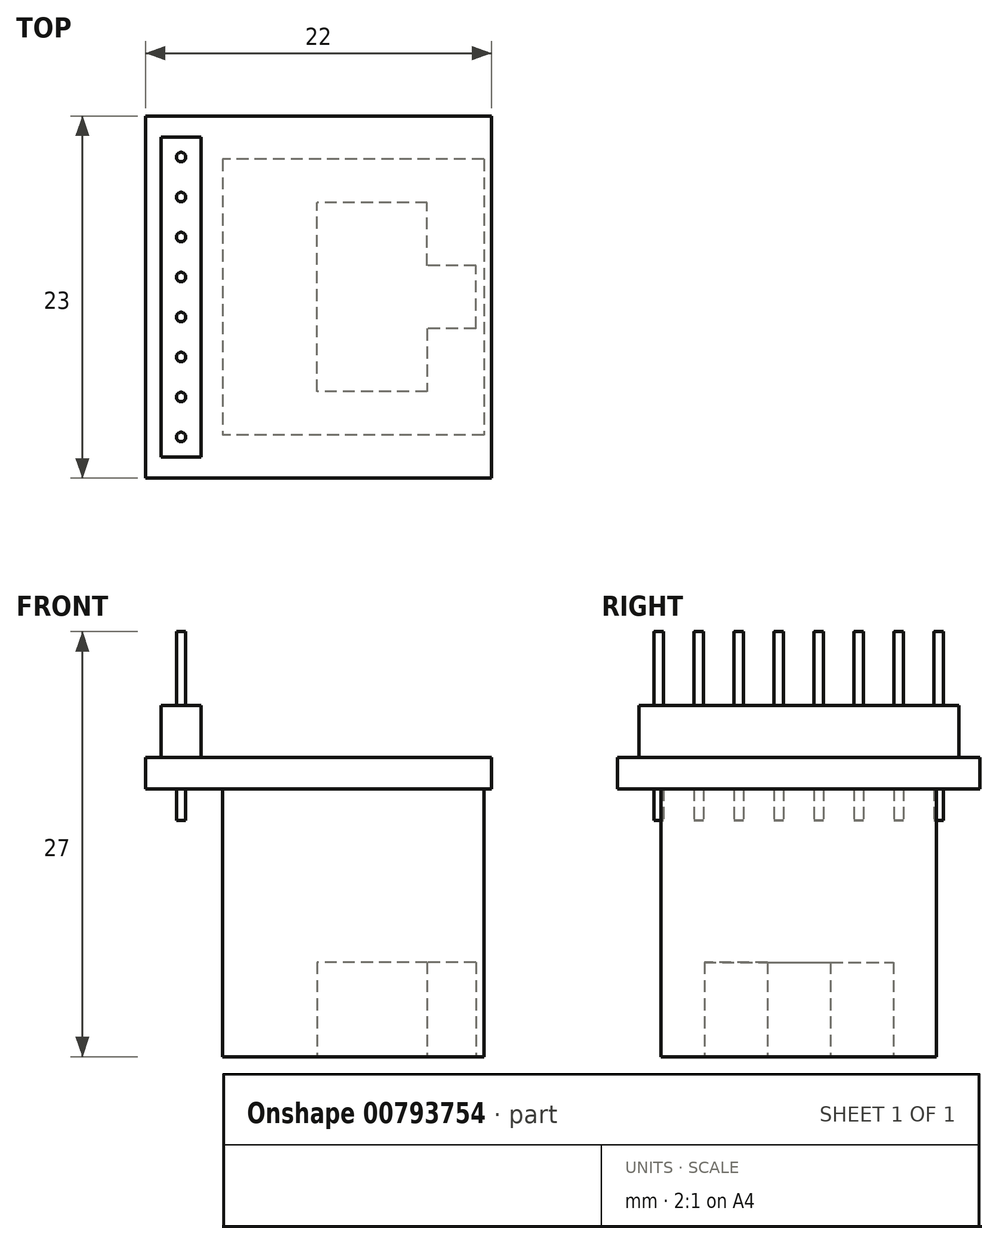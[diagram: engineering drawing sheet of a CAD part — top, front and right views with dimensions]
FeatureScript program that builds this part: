
annotation { "Feature Type Name" : "Feature", "Feature Type Description" : "" }
export const myFeature = defineFeature(function(context is Context, id is Id, definition is map)
    precondition{}
    {
        {
            var Q0;
            Q0=qCreatedBy(makeId("Top.planeOp"),FACE);
            var sketch = newSketch(context, id + "F0", { "sketchPlane" : qUnion([Q0])});
            skLineSegment(sketch, "E0.bottom", {"start": v(8.3, 8.75) * mm, "end": v(-8.3, 8.75) * mm});
            skLineSegment(sketch, "E0.top", {"start": v(8.3, -8.75) * mm, "end": v(-8.3, -8.75) * mm});
            skLineSegment(sketch, "E0.left", {"start": v(8.3, 8.75) * mm, "end": v(8.3, -8.75) * mm});
            skLineSegment(sketch, "E0.right", {"start": v(-8.3, 8.75) * mm, "end": v(-8.3, -8.75) * mm});
            skPoint(sketch, "E0.middle", {"position": v(0, 0) * mm});
            skSolve(sketch);
        }
        {
            var Q0;
            Q0=makeQuery(id+"F0.imprint","IMPRINT",FACE,{"disambiguationData":[TD([[makeQuery(id+"F0.imprint","IMPRINT",EDGE,{"derivedFrom":sQuery(id+"F0.wireOp",EDGE,"E0.bottom")}),1.0]])]});
            extrude(context, id + "F1", {"entities" : qUnion([Q0]), "depth" : 17 * mm, "offsetDistance" : 25 * mm});
        }
        {
            var Q0;
            Q0=makeQuery(id+"F1.opExtrude","CAP_FACE",FACE,{"disambiguationData":[OSD([sQuery(id+"F0.wireOp",EDGE,"E0.bottom"),sQuery(id+"F0.wireOp",EDGE,"E0.top"),sQuery(id+"F0.wireOp",EDGE,"E0.left"),sQuery(id+"F0.wireOp",EDGE,"E0.right")])],"isStart":true});
            var sketch = newSketch(context, id + "F2", { "sketchPlane" : qUnion([Q0])});
            skLineSegment(sketch, "E1", {"start": v(8.3, 0) * mm, "end": v(-8.3, 0) * mm, "construction": true});
            skLineSegment(sketch, "E2", {"start": v(7.8, 0) * mm, "end": v(7.8, -2) * mm});
            skLineSegment(sketch, "E3", {"start": v(7.8, -2) * mm, "end": v(4.7, -2) * mm});
            skLineSegment(sketch, "E4", {"start": v(4.7, -2) * mm, "end": v(4.7, -6) * mm});
            skLineSegment(sketch, "E5", {"start": v(4.7, -6) * mm, "end": v(-2.3, -6) * mm});
            skLineSegment(sketch, "E6", {"start": v(-2.3, -6) * mm, "end": v(-2.3, 0) * mm});
            skLineSegment(sketch, "E7.MirrorCS", {"start": v(7.8, 0) * mm, "end": v(7.8, 2) * mm});
            skLineSegment(sketch, "E8.MirrorCS", {"start": v(7.8, 2) * mm, "end": v(4.7, 2) * mm});
            skLineSegment(sketch, "E9.MirrorCS", {"start": v(4.7, 2) * mm, "end": v(4.7, 6) * mm});
            skLineSegment(sketch, "E10.MirrorCS", {"start": v(4.7, 6) * mm, "end": v(-2.3, 6) * mm});
            skLineSegment(sketch, "E11.MirrorCS", {"start": v(-2.3, 6) * mm, "end": v(-2.3, 0) * mm});
            skSolve(sketch);
        }
        {
            var Q0;
            Q0=makeQuery(id+"F2.imprint","IMPRINT",FACE,{"disambiguationData":[TD([[makeQuery(id+"F2.imprint","IMPRINT",EDGE,{"derivedFrom":sQuery(id+"F2.wireOp",EDGE,"E2")}),-1.0]])]});
            extrude(context, id + "F3", {"entities" : qUnion([Q0]), "operationType" : NewBodyOperationType.REMOVE, "oppositeDirection" : true, "depth" : 6 * mm, "offsetDistance" : 25 * mm});
        }
        {
            var Q0;
            Q0=makeQuery(id+"F1.opExtrude","CAP_FACE",FACE,{"disambiguationData":[OSD([sQuery(id+"F0.wireOp",EDGE,"E0.bottom"),sQuery(id+"F0.wireOp",EDGE,"E0.top"),sQuery(id+"F0.wireOp",EDGE,"E0.left"),sQuery(id+"F0.wireOp",EDGE,"E0.right")])],"isStart":false});
            var sketch = newSketch(context, id + "F4", { "sketchPlane" : qUnion([Q0])});
            skLineSegment(sketch, "E12.bottom", {"start": v(-13.2, 11.5) * mm, "end": v(8.8, 11.5) * mm});
            skLineSegment(sketch, "E12.top", {"start": v(-13.2, -11.5) * mm, "end": v(8.8, -11.5) * mm});
            skLineSegment(sketch, "E12.left", {"start": v(-13.2, 11.5) * mm, "end": v(-13.2, -11.5) * mm});
            skLineSegment(sketch, "E12.right", {"start": v(8.8, 11.5) * mm, "end": v(8.8, -11.5) * mm});
            skPoint(sketch, "E12.middle", {"position": v(-2.2, 0) * mm});
            skPoint(sketch, "E12.middle.positionSnap0", {"position": v(-8.3, 0) * mm});
            skPoint(sketch, "E12.centerSnap0", {"position": v(-8.3, 0) * mm});
            skSolve(sketch);
        }
        {
            var Q0;
            Q0=makeQuery(id+"F4.imprint","IMPRINT",FACE,{"disambiguationData":[TD([[makeQuery(id+"F4.imprint","IMPRINT",EDGE,{"derivedFrom":sQuery(id+"F4.wireOp",EDGE,"E12.bottom")}),-1.0]])]});
            var Q1;
            Q1=makeQuery(id+"F4.imprint","IMPRINT",FACE,{"disambiguationData":[TD([[makeQuery(id+"F4.imprint","IMPRINT",EDGE,{"derivedFrom":makeQuery(id+"F1.opExtrude","CAP_EDGE",EDGE,{"disambiguationData":[OSD([sQuery(id+"F0.wireOp",EDGE,"E0.bottom")])],"isStart":false})}),1.0]])]});
            extrude(context, id + "F5", {"entities" : qUnion([Q0, Q1]), "operationType" : NewBodyOperationType.ADD, "depth" : 2 * mm, "offsetDistance" : 25 * mm});
        }
        {
            var Q0;
            Q0=makeQuery(id+"F5.opExtrude","CAP_FACE",FACE,{"disambiguationData":[OSD([sQuery(id+"F4.wireOp",EDGE,"E12.bottom"),sQuery(id+"F4.wireOp",EDGE,"E12.top"),sQuery(id+"F4.wireOp",EDGE,"E12.left"),sQuery(id+"F4.wireOp",EDGE,"E12.right")])],"isStart":false});
            var sketch = newSketch(context, id + "F6", { "sketchPlane" : qUnion([Q0])});
            skLineSegment(sketch, "E13.bottom", {"start": v(-9.66, -7.62) * mm, "end": v(-12.2, -7.62) * mm});
            skLineSegment(sketch, "E13.top", {"start": v(-9.66, -10.16) * mm, "end": v(-12.2, -10.16) * mm});
            skLineSegment(sketch, "E13.left", {"start": v(-9.66, -7.62) * mm, "end": v(-9.66, -10.16) * mm});
            skLineSegment(sketch, "E13.right", {"start": v(-12.2, -7.62) * mm, "end": v(-12.2, -10.16) * mm});
            skPoint(sketch, "E13.middle", {"position": v(-10.93, -8.9) * mm});
            skCircle(sketch, "E14", {"center": v(-10.93, -8.9) * mm, "radius": 0.3 * mm});
            skPoint(sketch, "E15.0.1.0", {"position": v(-10.93, -6.35) * mm});
            skCircle(sketch, "E15.0.1.1", {"center": v(-10.93, -6.35) * mm, "radius": 0.3 * mm});
            skLineSegment(sketch, "E15.0.1.3", {"start": v(-12.2, -5.08) * mm, "end": v(-12.2, -7.62) * mm});
            skLineSegment(sketch, "E15.0.1.4", {"start": v(-9.66, -5.08) * mm, "end": v(-9.66, -7.62) * mm});
            skPoint(sketch, "E15.0.2.0", {"position": v(-10.93, -3.81) * mm});
            skCircle(sketch, "E15.0.2.1", {"center": v(-10.93, -3.81) * mm, "radius": 0.3 * mm});
            skLineSegment(sketch, "E15.0.2.2", {"start": v(-9.66, -5.08) * mm, "end": v(-12.2, -5.08) * mm});
            skLineSegment(sketch, "E15.0.2.3", {"start": v(-12.2, -2.54) * mm, "end": v(-12.2, -5.08) * mm});
            skLineSegment(sketch, "E15.0.2.4", {"start": v(-9.66, -2.54) * mm, "end": v(-9.66, -5.08) * mm});
            skPoint(sketch, "E15.0.3.0", {"position": v(-10.93, -1.27) * mm});
            skCircle(sketch, "E15.0.3.1", {"center": v(-10.93, -1.27) * mm, "radius": 0.3 * mm});
            skLineSegment(sketch, "E15.0.3.2", {"start": v(-9.66, -2.54) * mm, "end": v(-12.2, -2.54) * mm});
            skLineSegment(sketch, "E15.0.3.3", {"start": v(-12.2, 0) * mm, "end": v(-12.2, -2.54) * mm});
            skLineSegment(sketch, "E15.0.3.4", {"start": v(-9.66, 0) * mm, "end": v(-9.66, -2.54) * mm});
            skPoint(sketch, "E15.0.4.0", {"position": v(-10.93, 1.27) * mm});
            skCircle(sketch, "E15.0.4.1", {"center": v(-10.93, 1.27) * mm, "radius": 0.3 * mm});
            skLineSegment(sketch, "E15.0.4.2", {"start": v(-9.66, 0) * mm, "end": v(-12.2, 0) * mm});
            skLineSegment(sketch, "E15.0.4.3", {"start": v(-12.2, 2.54) * mm, "end": v(-12.2, 0) * mm});
            skLineSegment(sketch, "E15.0.4.4", {"start": v(-9.66, 2.54) * mm, "end": v(-9.66, 0) * mm});
            skPoint(sketch, "E15.0.5.0", {"position": v(-10.93, 3.8) * mm});
            skCircle(sketch, "E15.0.5.1", {"center": v(-10.93, 3.8) * mm, "radius": 0.3 * mm});
            skLineSegment(sketch, "E15.0.5.2", {"start": v(-9.66, 2.54) * mm, "end": v(-12.2, 2.54) * mm});
            skLineSegment(sketch, "E15.0.5.3", {"start": v(-12.2, 5.08) * mm, "end": v(-12.2, 2.54) * mm});
            skLineSegment(sketch, "E15.0.5.4", {"start": v(-9.66, 5.08) * mm, "end": v(-9.66, 2.54) * mm});
            skPoint(sketch, "E15.0.6.0", {"position": v(-10.93, 6.35) * mm});
            skCircle(sketch, "E15.0.6.1", {"center": v(-10.93, 6.35) * mm, "radius": 0.3 * mm});
            skLineSegment(sketch, "E15.0.6.2", {"start": v(-9.66, 5.08) * mm, "end": v(-12.2, 5.08) * mm});
            skLineSegment(sketch, "E15.0.6.3", {"start": v(-12.2, 7.62) * mm, "end": v(-12.2, 5.08) * mm});
            skLineSegment(sketch, "E15.0.6.4", {"start": v(-9.66, 7.62) * mm, "end": v(-9.66, 5.08) * mm});
            skPoint(sketch, "E15.0.7.0", {"position": v(-10.93, 8.89) * mm});
            skCircle(sketch, "E15.0.7.1", {"center": v(-10.93, 8.89) * mm, "radius": 0.3 * mm});
            skLineSegment(sketch, "E15.0.7.2", {"start": v(-9.66, 7.62) * mm, "end": v(-12.2, 7.62) * mm});
            skLineSegment(sketch, "E15.0.7.3", {"start": v(-12.2, 10.16) * mm, "end": v(-12.2, 7.62) * mm});
            skLineSegment(sketch, "E15.0.7.4", {"start": v(-9.66, 10.16) * mm, "end": v(-9.66, 7.62) * mm});
            skLineSegment(sketch, "E15.direction1", {"start": v(-12.2, -10.16) * mm, "end": v(-12.2, -10.16) * mm});
            skLineSegment(sketch, "E15.direction2", {"start": v(-12.2, -10.16) * mm, "end": v(-12.2, -7.62) * mm, "construction": true});
            skLineSegment(sketch, "E16", {"start": v(-12.2, 10.16) * mm, "end": v(-9.66, 10.16) * mm});
            skLineSegment(sketch, "E17", {"start": v(-9.66, -10.16) * mm, "end": v(-9.66, -11.5) * mm, "construction": true});
            skLineSegment(sketch, "E18", {"start": v(-12.2, 10.16) * mm, "end": v(-12.2, 11.5) * mm, "construction": true});
            skSolve(sketch);
        }
        {
            var Q0;
            Q0=makeQuery(id+"F6.imprint","IMPRINT",FACE,{"disambiguationData":[TD([[makeQuery(id+"F6.imprint","IMPRINT",EDGE,{"derivedFrom":sQuery(id+"F6.wireOp",EDGE,"E13.top")}),-1.0]])]});
            var Q1;
            Q1=makeQuery(id+"F6.imprint","IMPRINT",FACE,{"disambiguationData":[TD([[makeQuery(id+"F6.imprint","IMPRINT",EDGE,{"derivedFrom":sQuery(id+"F6.wireOp",EDGE,"E15.0.1.1")}),-1.0]])]});
            var Q2;
            Q2=makeQuery(id+"F6.imprint","IMPRINT",FACE,{"disambiguationData":[TD([[makeQuery(id+"F6.imprint","IMPRINT",EDGE,{"derivedFrom":sQuery(id+"F6.wireOp",EDGE,"E15.0.2.1")}),-1.0]])]});
            var Q3;
            Q3=makeQuery(id+"F6.imprint","IMPRINT",FACE,{"disambiguationData":[TD([[makeQuery(id+"F6.imprint","IMPRINT",EDGE,{"derivedFrom":sQuery(id+"F6.wireOp",EDGE,"E15.0.3.1")}),-1.0]])]});
            var Q4;
            Q4=makeQuery(id+"F6.imprint","IMPRINT",FACE,{"disambiguationData":[TD([[makeQuery(id+"F6.imprint","IMPRINT",EDGE,{"derivedFrom":sQuery(id+"F6.wireOp",EDGE,"E15.0.4.1")}),-1.0]])]});
            var Q5;
            Q5=makeQuery(id+"F6.imprint","IMPRINT",FACE,{"disambiguationData":[TD([[makeQuery(id+"F6.imprint","IMPRINT",EDGE,{"derivedFrom":sQuery(id+"F6.wireOp",EDGE,"E15.0.7.1")}),-1.0]])]});
            var Q6;
            Q6=makeQuery(id+"F6.imprint","IMPRINT",FACE,{"disambiguationData":[TD([[makeQuery(id+"F6.imprint","IMPRINT",EDGE,{"derivedFrom":sQuery(id+"F6.wireOp",EDGE,"E15.0.5.1")}),-1.0]])]});
            var Q7;
            Q7=makeQuery(id+"F6.imprint","IMPRINT",FACE,{"disambiguationData":[TD([[makeQuery(id+"F6.imprint","IMPRINT",EDGE,{"derivedFrom":sQuery(id+"F6.wireOp",EDGE,"E15.0.6.1")}),-1.0]])]});
            extrude(context, id + "F7", {"entities" : qUnion([Q0, Q1, Q2, Q3, Q4, Q5, Q6, Q7]), "operationType" : NewBodyOperationType.ADD, "depth" : 3.3 * mm, "offsetDistance" : 25 * mm});
        }
        {
            var Q0;
            Q0=makeQuery(id+"F6.imprint","IMPRINT",FACE,{"disambiguationData":[TD([[makeQuery(id+"F6.imprint","IMPRINT",EDGE,{"derivedFrom":sQuery(id+"F6.wireOp",EDGE,"E14")}),1.0]])]});
            var Q1;
            Q1=makeQuery(id+"F6.imprint","IMPRINT",FACE,{"disambiguationData":[TD([[makeQuery(id+"F6.imprint","IMPRINT",EDGE,{"derivedFrom":sQuery(id+"F6.wireOp",EDGE,"E15.0.1.1")}),1.0]])]});
            var Q2;
            Q2=makeQuery(id+"F6.imprint","IMPRINT",FACE,{"disambiguationData":[TD([[makeQuery(id+"F6.imprint","IMPRINT",EDGE,{"derivedFrom":sQuery(id+"F6.wireOp",EDGE,"E15.0.2.1")}),1.0]])]});
            var Q3;
            Q3=makeQuery(id+"F6.imprint","IMPRINT",FACE,{"disambiguationData":[TD([[makeQuery(id+"F6.imprint","IMPRINT",EDGE,{"derivedFrom":sQuery(id+"F6.wireOp",EDGE,"E15.0.3.1")}),1.0]])]});
            var Q4;
            Q4=makeQuery(id+"F6.imprint","IMPRINT",FACE,{"disambiguationData":[TD([[makeQuery(id+"F6.imprint","IMPRINT",EDGE,{"derivedFrom":sQuery(id+"F6.wireOp",EDGE,"E15.0.4.1")}),1.0]])]});
            var Q5;
            Q5=makeQuery(id+"F6.imprint","IMPRINT",FACE,{"disambiguationData":[TD([[makeQuery(id+"F6.imprint","IMPRINT",EDGE,{"derivedFrom":sQuery(id+"F6.wireOp",EDGE,"E15.0.5.1")}),1.0]])]});
            var Q6;
            Q6=makeQuery(id+"F6.imprint","IMPRINT",FACE,{"disambiguationData":[TD([[makeQuery(id+"F6.imprint","IMPRINT",EDGE,{"derivedFrom":sQuery(id+"F6.wireOp",EDGE,"E15.0.6.1")}),1.0]])]});
            var Q7;
            Q7=makeQuery(id+"F6.imprint","IMPRINT",FACE,{"disambiguationData":[TD([[makeQuery(id+"F6.imprint","IMPRINT",EDGE,{"derivedFrom":sQuery(id+"F6.wireOp",EDGE,"E15.0.7.1")}),1.0]])]});
            extrude(context, id + "F8", {"entities" : qUnion([Q0, Q1, Q2, Q3, Q4, Q5, Q6, Q7]), "operationType" : NewBodyOperationType.ADD, "depth" : 8 * mm, "offsetDistance" : 25 * mm, "hasSecondDirection" : true, "secondDirectionOppositeDirection" : true, "secondDirectionDepth" : 4 * mm});
        }
    });
